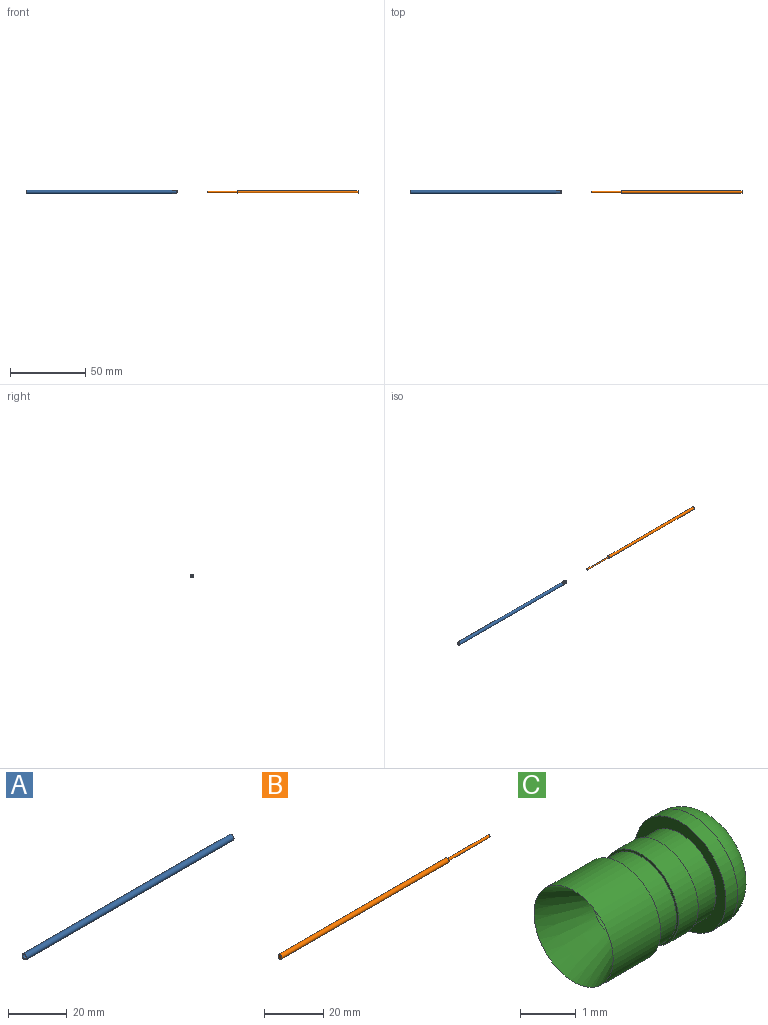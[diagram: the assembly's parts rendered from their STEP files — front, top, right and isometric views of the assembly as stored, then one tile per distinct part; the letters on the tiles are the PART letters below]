
ASSEMBLY  parts=3 mates=2
PART A: 4 faces, bbox 100x2.3x2.3 mm
  f0: plane 2.3x2.3mm, normal (-1,0,0), area 1.6mm2, adj f1,f3
  f1: cylinder r=0.9mm len=100mm, axis (-1,0,0), area 565.5mm2, adj f0,f2
  f2: plane 2.3x2.3mm, normal (1,0,0), area 1.6mm2, adj f1,f3
  f3: cylinder r=1.15mm len=100mm, axis (-1,0,0), area 722.6mm2, adj f0,f2
PART B: 5 faces, bbox 100x1.8x1.8 mm
  f0: plane 1.8x1.8mm, normal (-1,0,0), area 2.5mm2, adj f4
  f1: plane 1x1mm, normal (1,0,0), area 0.8mm2, adj f2
  f2: cylinder r=0.5mm len=20mm, axis (-1,0,0), area 62.8mm2, adj f1,f3
  f3: plane 1.8x1.8mm, normal (1,0,0), area 1.8mm2, adj f2,f4
  f4: cylinder r=0.9mm len=80mm, axis (-1,0,0), area 452.4mm2, adj f0,f3
PART C: 13 faces, bbox 3.5x2.5x2.5 mm
  f0: cylinder r=1.15mm len=2.3mm, axis (-1,0,0), area 2.2mm2, adj f1,f12
  f1: plane 2.3x2.3mm, normal (-1,0,0), area 1.6mm2, adj f0,f2
  f2: cylinder r=0.9mm len=1.8mm, axis (-1,0,0), area 2.8mm2, adj f1,f3
  f3: plane 1.9x1.9mm, normal (1,0,0), area 0.3mm2, adj f2,f4
  f4: cylinder r=0.95mm len=1.9mm, axis (-1,0,0), area 3mm2, adj f3,f5
  f5: plane 1.9x1.9mm, normal (-1,0,0), area 0.3mm2, adj f4,f6
  f6: cylinder r=0.9mm len=1.8mm, axis (-1,0,0), area 2.8mm2, adj f5,f7
  f7: plane 2x2mm, normal (1,0,0), area 0.6mm2, adj f6,f8
  f8: cylinder r=1mm len=2mm, axis (-1,0,0), area 7.5mm2, adj f7,f9
  f9: cone r=1mm half-angle=26.6deg, axis (-1,0,0), area 5.3mm2, adj f8,f10
  f10: cylinder r=0.5mm len=2.5mm, axis (-1,0,0), area 7.9mm2, adj f9,f11
  f11: plane 1.3x1.3mm, normal (1,0,0), area 0.5mm2, adj f10,f12
  f12: torus R=0.65mm, axis (-1,0,0), area 4.8mm2, adj f0,f11
PLACE A t=(-90.33,15.42,24.99)mm
PLACE B rot(axis=(0,0,-1),180deg) t=(45.73,15.42,24.99)mm
PLACE C t=(3.32,15.42,24.99)mm
MATE slider B.f2 <-> C.f0  axis (1,0,0) through (35.73,15.42,24.99)mm
MATE slider C.f0 <-> A.f1  axis (1,0,0) through (3.19,15.42,24.99)mm
